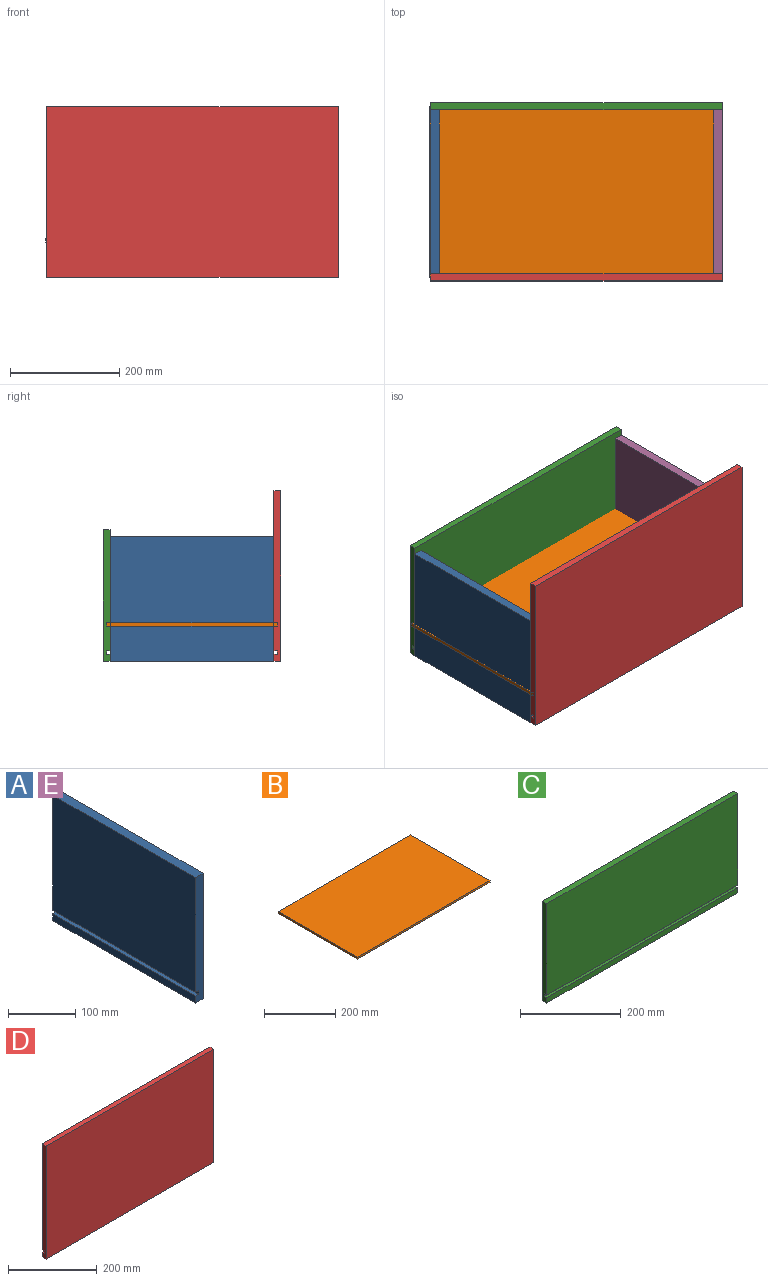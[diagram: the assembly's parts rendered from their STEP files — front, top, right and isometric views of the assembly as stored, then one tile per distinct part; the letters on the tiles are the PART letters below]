
ASSEMBLY  parts=5 mates=5
PART A: 10 faces, bbox 15.9x300.7x228.6 mm
  f0: plane 300.68x12.7mm, normal (-1,0,0), area 3818.6mm2, adj f1,f2,f3,f7
  f1: plane 228.6x15.88mm, normal (0,-1,0), area 3588.7mm2, adj f0,f2,f4,f5,f6,f7,f8,f9
  f2: plane 300.68x15.88mm, normal (0,0,-1), area 4773.2mm2, adj f0,f1,f3,f6
  f3: plane 228.6x15.88mm, normal (0,1,0), area 3588.7mm2, adj f0,f2,f4,f5,f6,f7,f8,f9
  f4: plane 300.68x15.88mm, normal (0,0,1), area 4773.2mm2, adj f1,f3,f5,f6
  f5: plane 300.68x209.55mm, normal (-1,0,0), area 63006.7mm2, adj f1,f3,f4,f8
  f6: plane 300.68x228.6mm, normal (1,0,0), area 68734.6mm2, adj f1,f2,f3,f4
  f7: plane 300.68x6.35mm, normal (0,0,1), area 1909.3mm2, adj f0,f1,f3,f9
  f8: plane 300.68x6.35mm, normal (0,0,-1), area 1909.3mm2, adj f1,f3,f5,f9
  f9: plane 300.68x6.35mm, normal (-1,0,0), area 1909.3mm2, adj f1,f3,f7,f8
PART B: 6 faces, bbox 527.1x313.4x6.4 mm
  f0: plane 527.05x313.38mm, normal (0,0,-1), area 165164.9mm2, adj f1,f3,f4,f5
  f1: plane 527.05x6.35mm, normal (0,1,0), area 3346.8mm2, adj f0,f2,f4,f5
  f2: plane 527.05x313.38mm, normal (0,0,1), area 165164.9mm2, adj f1,f3,f4,f5
  f3: plane 527.05x6.35mm, normal (0,-1,0), area 3346.8mm2, adj f0,f2,f4,f5
  f4: plane 313.38x6.35mm, normal (-1,0,0), area 1989.9mm2, adj f0,f1,f2,f3
  f5: plane 313.38x6.35mm, normal (1,0,0), area 1989.9mm2, adj f0,f1,f2,f3
PART C: 10 faces, bbox 535x12.7x241.3 mm
  f0: plane 534.99x222.25mm, normal (0,-1,0), area 118901mm2, adj f1,f2,f6,f8
  f1: plane 241.3x12.7mm, normal (-1,0,0), area 3024.2mm2, adj f0,f3,f4,f5,f6,f7,f8,f9
  f2: plane 241.3x12.7mm, normal (1,0,0), area 3024.2mm2, adj f0,f3,f4,f5,f6,f7,f8,f9
  f3: plane 534.99x12.7mm, normal (0,-1,0), area 6794.3mm2, adj f1,f2,f4,f7
  f4: plane 534.99x12.7mm, normal (0,0,-1), area 6794.3mm2, adj f1,f2,f3,f5
  f5: plane 534.99x241.3mm, normal (0,1,0), area 129092.5mm2, adj f1,f2,f4,f6
  f6: plane 534.99x12.7mm, normal (0,0,1), area 6794.3mm2, adj f0,f1,f2,f5
  f7: plane 534.99x6.35mm, normal (0,0,1), area 3397.2mm2, adj f1,f2,f3,f9
  f8: plane 534.99x6.35mm, normal (0,0,-1), area 3397.2mm2, adj f0,f1,f2,f9
  f9: plane 534.99x6.35mm, normal (0,-1,0), area 3397.2mm2, adj f1,f2,f7,f8
PART D: 10 faces, bbox 535x12.7x312.7 mm
  f0: plane 534.99x293.69mm, normal (0,1,0), area 157119.1mm2, adj f1,f2,f4,f8
  f1: plane 312.74x12.7mm, normal (-1,0,0), area 3931.4mm2, adj f0,f3,f4,f5,f6,f7,f8,f9
  f2: plane 312.74x12.7mm, normal (1,0,0), area 3931.4mm2, adj f0,f3,f4,f5,f6,f7,f8,f9
  f3: plane 534.99x12.7mm, normal (0,0,-1), area 6794.3mm2, adj f1,f2,f5,f6
  f4: plane 534.99x12.7mm, normal (0,0,1), area 6794.3mm2, adj f0,f1,f2,f6
  f5: plane 534.99x12.7mm, normal (0,1,0), area 6794.3mm2, adj f1,f2,f3,f7
  f6: plane 534.99x312.74mm, normal (0,-1,0), area 167310.7mm2, adj f1,f2,f3,f4
  f7: plane 534.99x6.35mm, normal (0,0,1), area 3397.2mm2, adj f1,f2,f5,f9
  f8: plane 534.99x6.35mm, normal (0,0,-1), area 3397.2mm2, adj f0,f1,f2,f9
  f9: plane 534.99x6.35mm, normal (0,1,0), area 3397.2mm2, adj f1,f2,f7,f8
PART E: same geometry as A
PLACE A rot(axis=(0,0,-1),180deg) t=(549.15,319.94,-83.2)mm
PLACE B t=(-20.77,-6.13,-31.51)mm fixed
PLACE C t=(-11.24,-6.13,-83.2)mm
PLACE D t=(-11.24,-6.13,-83.2)mm
PLACE E t=(-11.24,-6.13,-83.2)mm
MATE planar B.f3 <-> D.f9  axis (0,-1,0) through (263.4,0.22,-2.93)mm
MATE fastened D.f3 <-> E.f2  axis (0,0,-1) through (536.45,6.57,-70.5)mm
MATE fastened D.f1 <-> A.f6  axis (-1,0,0) through (1.46,6.57,-70.5)mm
MATE fastened E.f6 <-> C.f2  axis (1,0,0) through (536.45,307.24,-70.5)mm
MATE planar B.f5 <-> E.f9  axis (1,0,0) through (526.92,156.91,-2.93)mm
